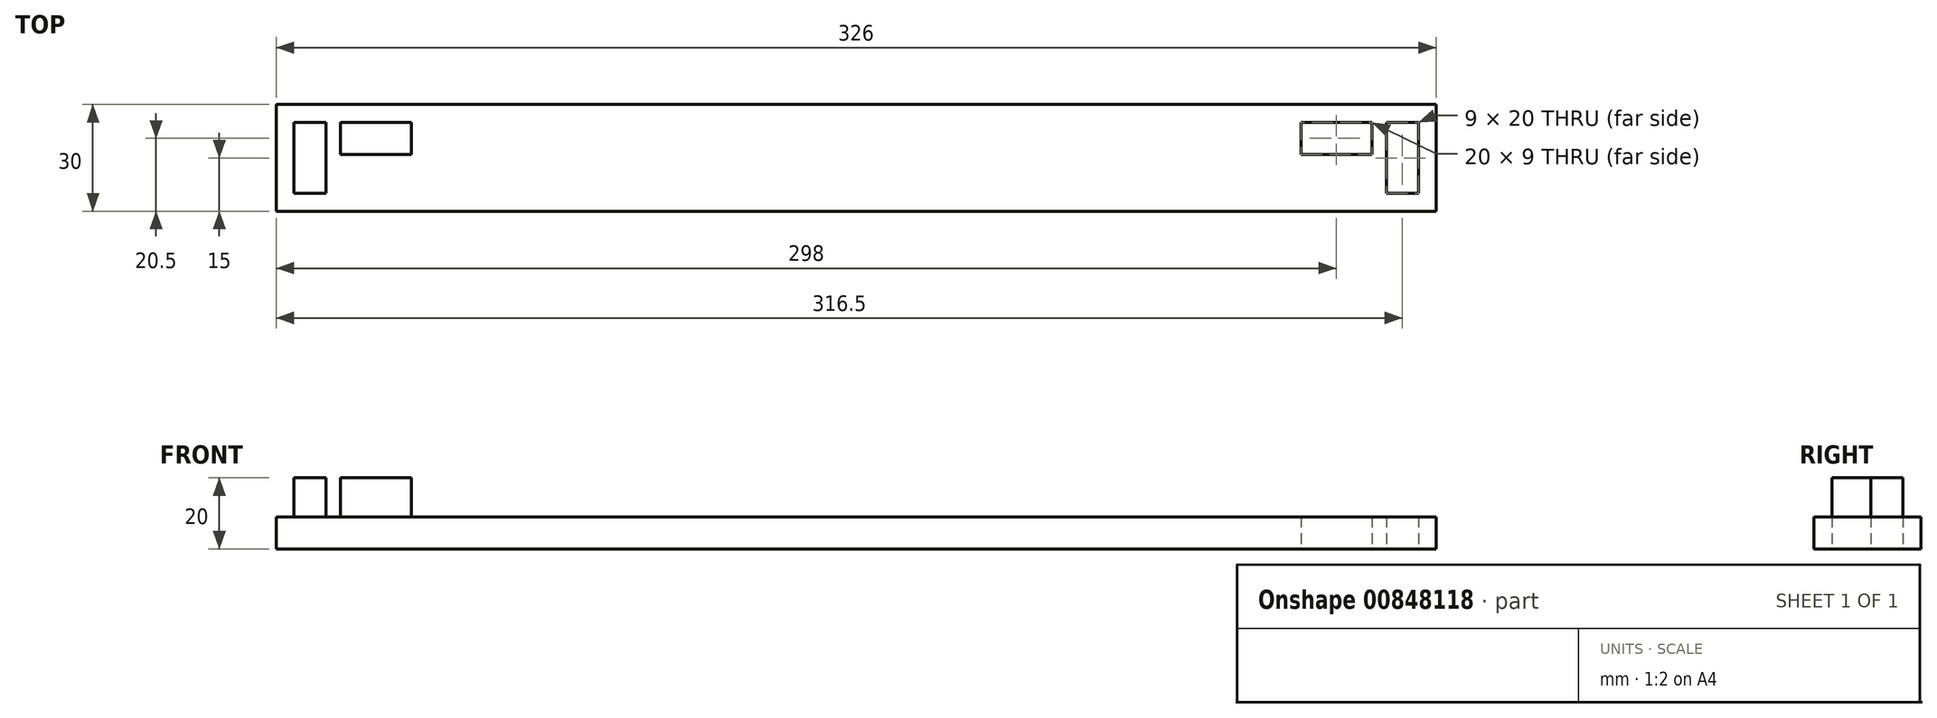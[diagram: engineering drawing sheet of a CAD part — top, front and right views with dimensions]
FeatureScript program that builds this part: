
annotation { "Feature Type Name" : "Feature", "Feature Type Description" : "" }
export const myFeature = defineFeature(function(context is Context, id is Id, definition is map)
    precondition{}
    {
        {
            var Q0;
            Q0=qCreatedBy(makeId("Top.planeOp"),FACE);
            var sketch = newSketch(context, id + "F0", { "sketchPlane" : qUnion([Q0])});
            skLineSegment(sketch, "E0.bottom", {"start": v(-163, 15) * mm, "end": v(0, 15) * mm});
            skLineSegment(sketch, "E0.top", {"start": v(-163, -15) * mm, "end": v(0, -15) * mm});
            skLineSegment(sketch, "E0.left", {"start": v(-163, 15) * mm, "end": v(-163, -15) * mm});
            skLineSegment(sketch, "E0.right", {"start": v(0, 15) * mm, "end": v(0, -15) * mm});
            skPoint(sketch, "E0.middle", {"position": v(-81.5, 0) * mm});
            skLineSegment(sketch, "E1.bottom", {"start": v(-149, 10) * mm, "end": v(-158, 10) * mm});
            skLineSegment(sketch, "E1.top", {"start": v(-149, -10) * mm, "end": v(-158, -10) * mm});
            skLineSegment(sketch, "E1.left", {"start": v(-149, 10) * mm, "end": v(-149, -10) * mm});
            skLineSegment(sketch, "E1.right", {"start": v(-158, 10) * mm, "end": v(-158, -10) * mm});
            skPoint(sketch, "E1.middle", {"position": v(-153.5, 0) * mm});
            skLineSegment(sketch, "E2.bottom", {"start": v(-125, 10) * mm, "end": v(-145, 10) * mm});
            skLineSegment(sketch, "E2.top", {"start": v(-125, 1) * mm, "end": v(-145, 1) * mm});
            skLineSegment(sketch, "E2.left", {"start": v(-145, 10) * mm, "end": v(-145, 1) * mm});
            skLineSegment(sketch, "E2.right", {"start": v(-125, 10) * mm, "end": v(-125, 1) * mm});
            skPoint(sketch, "E2.middle", {"position": v(-135, 5.5) * mm});
            skSolve(sketch);
        }
        {
            var Q0;
            Q0=makeQuery(id+"F0.imprint","IMPRINT",FACE,{"disambiguationData":[TD([[makeQuery(id+"F0.imprint","IMPRINT",EDGE,{"derivedFrom":sQuery(id+"F0.wireOp",EDGE,"E0.bottom")}),-1.0]])]});
            extrude(context, id + "F1", {"entities" : qUnion([Q0]), "depth" : 9 * mm, "offsetDistance" : 25 * mm});
        }
        {
            var Q0;
            Q0=makeQuery(id+"F0.imprint","IMPRINT",FACE,{"disambiguationData":[TD([[makeQuery(id+"F0.imprint","IMPRINT",EDGE,{"derivedFrom":sQuery(id+"F0.wireOp",EDGE,"E1.bottom")}),1.0]])]});
            var Q1;
            Q1=makeQuery(id+"F0.imprint","IMPRINT",FACE,{"disambiguationData":[TD([[makeQuery(id+"F0.imprint","IMPRINT",EDGE,{"derivedFrom":sQuery(id+"F0.wireOp",EDGE,"E2.bottom")}),1.0]])]});
            extrude(context, id + "F2", {"entities" : qUnion([Q0, Q1]), "depth" : 20 * mm, "offsetDistance" : 25 * mm});
        }
        {
            var Q0;
            Q0=makeQuery(id+"F1.opExtrude","SWEPT_BODY",BODY,{"disambiguationData":[OSD([sQuery(id+"F0.wireOp",EDGE,"E0.bottom"),sQuery(id+"F0.wireOp",EDGE,"E0.top"),sQuery(id+"F0.wireOp",EDGE,"E0.left"),sQuery(id+"F0.wireOp",EDGE,"E0.right"),sQuery(id+"F0.wireOp",EDGE,"E1.bottom"),sQuery(id+"F0.wireOp",EDGE,"E1.top"),sQuery(id+"F0.wireOp",EDGE,"E1.left"),sQuery(id+"F0.wireOp",EDGE,"E1.right"),sQuery(id+"F0.wireOp",EDGE,"E2.bottom"),sQuery(id+"F0.wireOp",EDGE,"E2.top"),sQuery(id+"F0.wireOp",EDGE,"E2.left"),sQuery(id+"F0.wireOp",EDGE,"E2.right")])]});
            var Q1;
            Q1=makeQuery(id+"F1.opExtrude","SWEPT_FACE",FACE,{"disambiguationData":[OSD([sQuery(id+"F0.wireOp",EDGE,"E0.right")])]});
            mirror(context, id + "F3", {"operationType" : NewBodyOperationType.ADD, "entities" : qUnion([Q0]), "mirrorPlane" : qUnion([Q1])});
        }
    });
